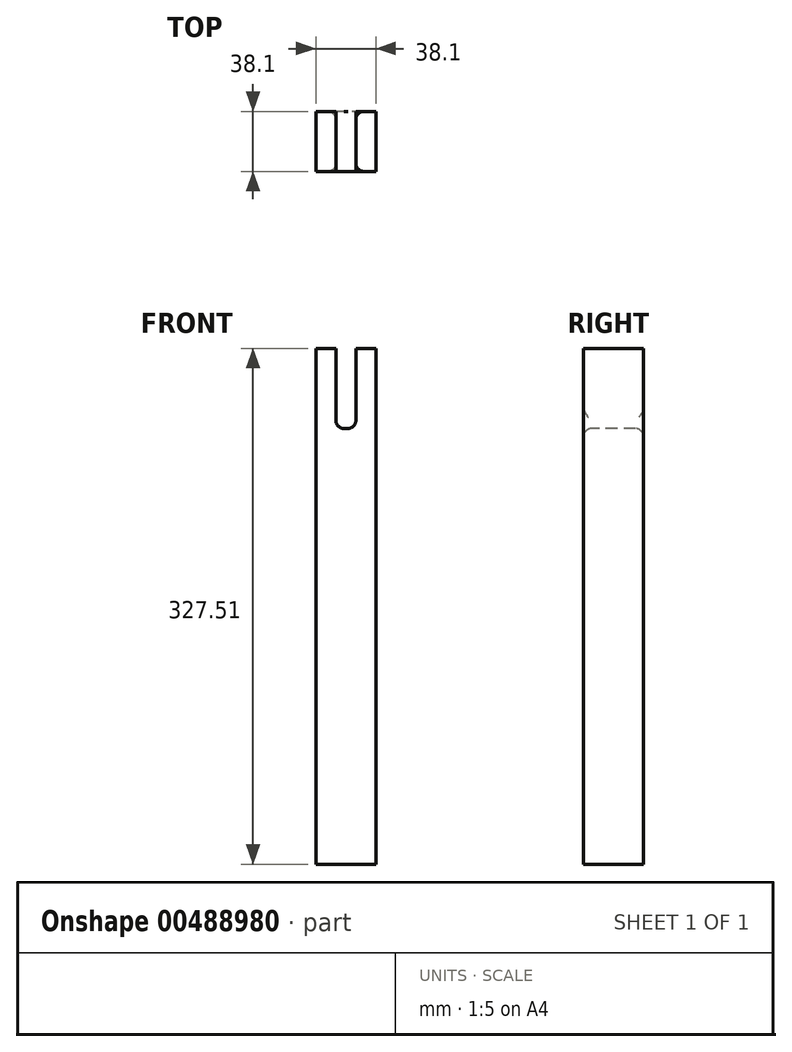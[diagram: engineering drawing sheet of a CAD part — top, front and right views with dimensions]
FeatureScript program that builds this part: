
annotation { "Feature Type Name" : "Feature", "Feature Type Description" : "" }
export const myFeature = defineFeature(function(context is Context, id is Id, definition is map)
    precondition{}
    {
        {
            var Q0;
            Q0=qCreatedBy(makeId("Top.planeOp"),FACE);
            var sketch = newSketch(context, id + "F0", { "sketchPlane" : qUnion([Q0])});
            skLineSegment(sketch, "E0.bottom", {"start": v(0, 0) * mm, "end": v(38.1, 0) * mm});
            skLineSegment(sketch, "E0.top", {"start": v(0, -38.1) * mm, "end": v(38.1, -38.1) * mm});
            skLineSegment(sketch, "E0.left", {"start": v(0, 0) * mm, "end": v(0, -38.1) * mm});
            skLineSegment(sketch, "E0.right", {"start": v(38.1, 0) * mm, "end": v(38.1, -38.1) * mm});
            skSolve(sketch);
        }
        {
            var Q0;
            Q0 = qSketchRegion(id + "F0", true);
            extrude(context, id + "F1", {"entities" : qUnion([Q0]), "depth" : 327.5 * mm, "offsetDistance" : 25.4 * mm});
        }
        {
            var Q0;
            Q0=makeQuery(id+"F1.opExtrude","CAP_FACE",FACE,{"disambiguationData":[OSD([sQuery(id+"F0.wireOp",EDGE,"E0.bottom"),sQuery(id+"F0.wireOp",EDGE,"E0.top"),sQuery(id+"F0.wireOp",EDGE,"E0.left"),sQuery(id+"F0.wireOp",EDGE,"E0.right")])],"isStart":false});
            var sketch = newSketch(context, id + "F2", { "sketchPlane" : qUnion([Q0])});
            skLineSegment(sketch, "E1", {"start": v(12.7, 0) * mm, "end": v(12.7, -38.1) * mm});
            skLineSegment(sketch, "E2", {"start": v(25.4, 0) * mm, "end": v(25.4, -38.1) * mm});
            skSolve(sketch);
        }
        {
            var Q0;
            {var subQ0=sQuery(id+"F2.wireOp",EDGE,"E1");Q0=makeQuery(id+"F2.imprint","IMPRINT",FACE,{"disambiguationData":[TD([[makeQuery(id+"F2.imprint","IMPRINT",EDGE,{"derivedFrom":subQ0}),1.0]])]});}
            extrude(context, id + "F3", {"entities" : qUnion([Q0]), "operationType" : NewBodyOperationType.REMOVE, "oppositeDirection" : true, "depth" : 50.8 * mm, "offsetDistance" : 25.4 * mm});
        }
        {
            var Q0;
            Q0=makeQuery(id+"F3.boolean.opBoolean","COPY",FACE,{"derivedFrom":makeQuery(id+"F3.opExtrude","CAP_FACE",FACE,{"disambiguationData":[OSD([sQuery(id+"F0.wireOp",EDGE,"E0.bottom"),sQuery(id+"F0.wireOp",EDGE,"E0.top"),sQuery(id+"F2.wireOp",EDGE,"E1"),sQuery(id+"F2.wireOp",EDGE,"E2")])],"isStart":false})});
            fillet(context, id + "F4", {"entities" : qUnion([Q0]), "radius" : 5.08 * mm, "tangentPropagation" : true, "allowEdgeOverflow" : false});
        }
    });
